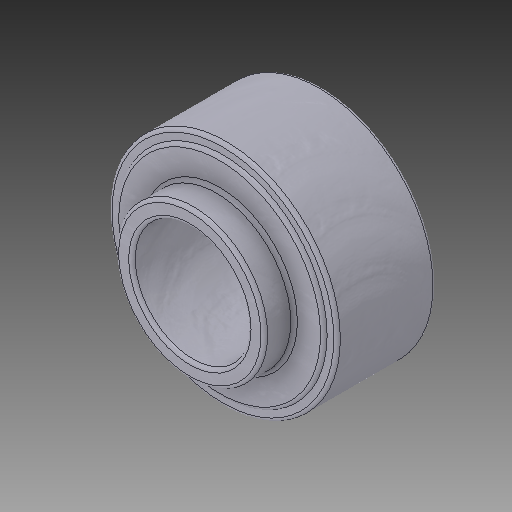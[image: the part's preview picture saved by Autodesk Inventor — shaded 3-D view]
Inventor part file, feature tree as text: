
AUTODESK INVENTOR PART (.ipt)
format: ipt  version: 2019 (Build 230136000, 136)  size: 220,672 bytes
history: native  units: in
note: dims shown in document units (in); Inventor stores cm internally (conversion verified against a paired STEP export)
features: sketch x6, other x3
ambient origin geometry x8: Origin, YZ Plane, XZ Plane, XY Plane, X Axis, Y Axis, Z Axis, Center Point
bodies: Solid1 (feature_tree)
feature tree (9):
  other  "project flange bearing part2_MIR2.ipt"
  other  "Solid1::project flange bearing part2_MIR2.ipt"
  other  "TaggingFeature1"
  sketch  "Sketch1"  dims[d0=0.3937in]
  sketch  "Sketch2"
  sketch  "Sketch3"
  sketch  "Sketch4"
  sketch  "Sketch5"
  sketch  "Sketch6"
